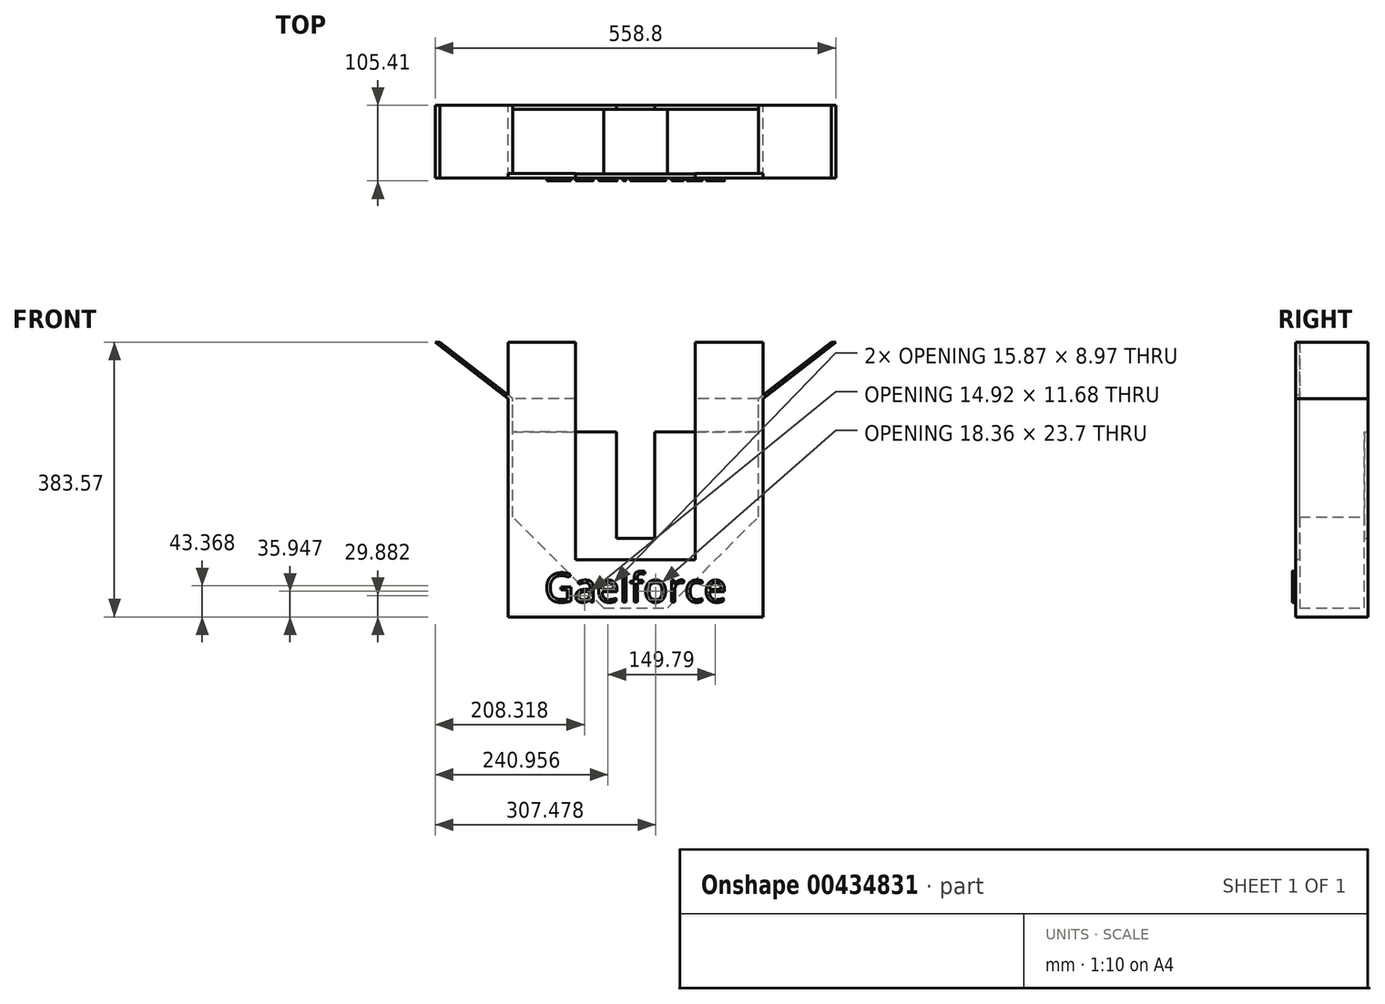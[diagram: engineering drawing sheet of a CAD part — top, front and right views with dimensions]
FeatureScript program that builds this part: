
annotation { "Feature Type Name" : "Feature", "Feature Type Description" : "" }
export const myFeature = defineFeature(function(context is Context, id is Id, definition is map)
    precondition{}
    {
        {
            var Q0;
            Q0=qCreatedBy(makeId("Front.planeOp"),FACE);
            var sketch = newSketch(context, id + "F0", { "sketchPlane" : qUnion([Q0])});
            skLineSegment(sketch, "E0.bottom", {"start": v(177.8, 152.4) * mm, "end": v(-177.8, 152.4) * mm});
            skLineSegment(sketch, "E0.top", {"start": v(177.8, -152.4) * mm, "end": v(-177.8, -152.4) * mm});
            skLineSegment(sketch, "E0.left", {"start": v(177.8, 152.4) * mm, "end": v(177.8, -152.4) * mm});
            skLineSegment(sketch, "E0.right", {"start": v(-177.8, 152.4) * mm, "end": v(-177.8, -152.4) * mm});
            skPoint(sketch, "E0.middle", {"position": v(0, 0) * mm});
            skSolve(sketch);
        }
        {
            var Q0;
            Q0=makeQuery(id+"F0.imprint","IMPRINT",FACE,{"disambiguationData":[TD([[makeQuery(id+"F0.imprint","IMPRINT",EDGE,{"derivedFrom":sQuery(id+"F0.wireOp",EDGE,"E0.bottom")}),1.0]])]});
            extrude(context, id + "F1", {"entities" : qUnion([Q0]), "endBound" : BoundingType.SYMMETRIC, "depth" : 101.6 * mm});
        }
        {
            var Q0;
            Q0=makeQuery(id+"F1.opExtrude","SWEPT_FACE",FACE,{"disambiguationData":[OSD([sQuery(id+"F0.wireOp",EDGE,"E0.bottom")])]});
            var sketch = newSketch(context, id + "F2", { "sketchPlane" : qUnion([Q0])});
            skLineSegment(sketch, "E1.bottom", {"start": v(-171.45, -44.94) * mm, "end": v(171.45, -44.94) * mm});
            skLineSegment(sketch, "E1.top", {"start": v(-171.45, 45.23) * mm, "end": v(171.45, 45.23) * mm});
            skLineSegment(sketch, "E1.left", {"start": v(-171.45, -44.94) * mm, "end": v(-171.45, 45.23) * mm});
            skLineSegment(sketch, "E1.right", {"start": v(171.45, -44.94) * mm, "end": v(171.45, 45.23) * mm});
            skSolve(sketch);
        }
        {
            var Q0;
            Q0=makeQuery(id+"F2.imprint","IMPRINT",FACE,{"disambiguationData":[TD([[makeQuery(id+"F2.imprint","IMPRINT",EDGE,{"derivedFrom":sQuery(id+"F2.wireOp",EDGE,"E1.bottom")}),1.0]])]});
            extrude(context, id + "F3", {"entities" : qUnion([Q0]), "operationType" : NewBodyOperationType.REMOVE, "oppositeDirection" : true, "depth" : 292.1 * mm});
        }
        {
            var Q0;
            Q0=makeQuery(id+"F1.opExtrude","SWEPT_FACE",FACE,{"disambiguationData":[OSD([sQuery(id+"F0.wireOp",EDGE,"E0.bottom")])]});
            var sketch = newSketch(context, id + "F4", { "sketchPlane" : qUnion([Q0])});
            skLineSegment(sketch, "E2", {"start": v(-171.45, 45.23) * mm, "end": v(-171.45, 50.8) * mm});
            skLineSegment(sketch, "E3", {"start": v(171.45, 45.23) * mm, "end": v(171.45, 50.8) * mm});
            skSolve(sketch);
        }
        {
            var Q0;
            {var subQ0=sQuery(id+"F4.wireOp",EDGE,"E2");Q0=makeQuery(id+"F4.imprint","IMPRINT",FACE,{"disambiguationData":[TD([[makeQuery(id+"F4.imprint","IMPRINT",EDGE,{"derivedFrom":subQ0}),-1.0]])]});}
            extrude(context, id + "F5", {"entities" : qUnion([Q0]), "operationType" : NewBodyOperationType.REMOVE, "oppositeDirection" : true, "depth" : 46.48 * mm});
        }
        {
            var Q0;
            Q0=makeQuery(id+"F1.opExtrude","CAP_FACE",FACE,{"disambiguationData":[OSD([sQuery(id+"F0.wireOp",EDGE,"E0.bottom"),sQuery(id+"F0.wireOp",EDGE,"E0.top"),sQuery(id+"F0.wireOp",EDGE,"E0.left"),sQuery(id+"F0.wireOp",EDGE,"E0.right")])],"isStart":false});
            var sketch = newSketch(context, id + "F6", { "sketchPlane" : qUnion([Q0])});
            skLineSegment(sketch, "E4.bottom", {"start": v(-83.6, -72.67) * mm, "end": v(83.6, -72.67) * mm});
            skLineSegment(sketch, "E4.top", {"start": v(-83.6, 377.47) * mm, "end": v(83.6, 377.47) * mm});
            skLineSegment(sketch, "E4.left", {"start": v(-83.6, -72.67) * mm, "end": v(-83.6, 377.47) * mm});
            skLineSegment(sketch, "E4.right", {"start": v(83.6, -72.67) * mm, "end": v(83.6, 377.47) * mm});
            skPoint(sketch, "E4.middle", {"position": v(0, 152.4) * mm});
            skSolve(sketch);
        }
        {
            var Q0;
            {var subQ0=sQuery(id+"F6.wireOp",EDGE,"E4.top");Q0=makeQuery(id+"F6.imprint","IMPRINT",FACE,{"disambiguationData":[TD([[makeQuery(id+"F6.imprint","IMPRINT",EDGE,{"derivedFrom":subQ0}),-1.0]])]});}
            var Q1;
            {var subQ0=sQuery(id+"F6.wireOp",EDGE,"E4.bottom");Q1=makeQuery(id+"F6.imprint","IMPRINT",FACE,{"disambiguationData":[TD([[makeQuery(id+"F6.imprint","IMPRINT",EDGE,{"derivedFrom":subQ0}),1.0]])]});}
            extrude(context, id + "F7", {"entities" : qUnion([Q0, Q1]), "operationType" : NewBodyOperationType.REMOVE, "oppositeDirection" : true, "depth" : 25.4 * mm});
        }
        {
            var Q0;
            Q0=makeQuery(id+"F1.opExtrude","CAP_FACE",FACE,{"disambiguationData":[OSD([sQuery(id+"F0.wireOp",EDGE,"E0.bottom"),sQuery(id+"F0.wireOp",EDGE,"E0.top"),sQuery(id+"F0.wireOp",EDGE,"E0.left"),sQuery(id+"F0.wireOp",EDGE,"E0.right")])],"isStart":false});
            var sketch = newSketch(context, id + "F8", { "sketchPlane" : qUnion([Q0])});
            skText(sketch, "E5", { "text": "Gaelforce", "fontName": "OpenSans-Regular.ttf"});
            const initialGuessF8  = {"E5": [-0.12725, -0.1316, 1, 0, 0.04083]};
            skSetInitialGuess(sketch, initialGuessF8);
            skSolve(sketch);
        }
        {
            var Q0;
            Q0 = qSketchRegion(id + "F8", true);
            extrude(context, id + "F9", {"entities" : qUnion([Q0]), "depth" : 3.8 * mm});
        }
        {
            var Q0;
            Q0=makeQuery(id+"F1.opExtrude","CAP_FACE",FACE,{"disambiguationData":[OSD([sQuery(id+"F0.wireOp",EDGE,"E0.bottom"),sQuery(id+"F0.wireOp",EDGE,"E0.top"),sQuery(id+"F0.wireOp",EDGE,"E0.left"),sQuery(id+"F0.wireOp",EDGE,"E0.right")])],"isStart":true});
            var sketch = newSketch(context, id + "F10", { "sketchPlane" : qUnion([Q0])});
            skLineSegment(sketch, "E6.bottom", {"start": v(-26.6, -43.01) * mm, "end": v(26.6, -43.01) * mm});
            skLineSegment(sketch, "E6.top", {"start": v(-26.6, 254.85) * mm, "end": v(26.6, 254.85) * mm});
            skLineSegment(sketch, "E6.left", {"start": v(-26.6, -43.01) * mm, "end": v(-26.6, 254.85) * mm});
            skLineSegment(sketch, "E6.right", {"start": v(26.6, -43.01) * mm, "end": v(26.6, 254.85) * mm});
            skPoint(sketch, "E6.middle", {"position": v(0, 105.92) * mm});
            skSolve(sketch);
        }
        {
            var Q0;
            {var subQ0=sQuery(id+"F10.wireOp",EDGE,"E6.bottom");Q0=makeQuery(id+"F10.imprint","IMPRINT",FACE,{"disambiguationData":[TD([[makeQuery(id+"F10.imprint","IMPRINT",EDGE,{"derivedFrom":subQ0}),1.0]])]});}
            extrude(context, id + "F11", {"entities" : qUnion([Q0]), "operationType" : NewBodyOperationType.REMOVE, "oppositeDirection" : true, "depth" : 25.4 * mm});
        }
        {
            var Q0;
            Q0=makeQuery(id+"F3.boolean.opBoolean","COPY",EDGE,{"derivedFrom":makeQuery(id+"F3.opExtrude","CAP_EDGE",EDGE,{"disambiguationData":[OSD([sQuery(id+"F2.wireOp",EDGE,"E1.left")])],"isStart":false})});
            var Q1;
            Q1=makeQuery(id+"F3.boolean.opBoolean","COPY",EDGE,{"derivedFrom":makeQuery(id+"F3.opExtrude","CAP_EDGE",EDGE,{"disambiguationData":[OSD([sQuery(id+"F2.wireOp",EDGE,"E1.right")])],"isStart":false})});
            chamfer(context, id + "F12", {"entities" : qUnion([Q0, Q1]), "width" : 127 * mm, "tangentPropagation" : true});
        }
        {
            var Q0;
            {var subQ0=sQuery(id+"F0.wireOp",EDGE,"E0.bottom");var subQ1=sQuery(id+"F0.wireOp",EDGE,"E0.left");var subQ2=sQuery(id+"F0.wireOp",EDGE,"E0.right");var subQ3=sQuery(id+"F0.wireOp",EDGE,"E0.top");Q0=makeQuery(id+"F9.boolean.opBoolean","SPLIT",FACE,{"disambiguationData":[TD([makeQuery(id+"F1.opExtrude","SWEPT_FACE",FACE,{"disambiguationData":[OSD([subQ0])]})])],"derivedFrom":makeQuery(id+"F1.opExtrude","CAP_FACE",FACE,{"disambiguationData":[OSD([subQ0,subQ3,subQ1,subQ2])],"isStart":false})});}
            var sketch = newSketch(context, id + "F13", { "sketchPlane" : qUnion([Q0])});
            skLineSegment(sketch, "E7.bottom", {"start": v(-279.4, 152.4) * mm, "end": v(279.4, 152.4) * mm});
            skLineSegment(sketch, "E7.top", {"start": v(-279.4, 231.17) * mm, "end": v(279.4, 231.17) * mm});
            skLineSegment(sketch, "E7.left", {"start": v(-279.4, 152.4) * mm, "end": v(-279.4, 231.17) * mm});
            skLineSegment(sketch, "E7.right", {"start": v(279.4, 152.4) * mm, "end": v(279.4, 231.17) * mm});
            skSolve(sketch);
        }
        {
            var Q0;
            Q0=makeQuery(id+"F13.imprint","IMPRINT",FACE,{"disambiguationData":[TD([[makeQuery(id+"F13.imprint","IMPRINT",EDGE,{"derivedFrom":sQuery(id+"F13.wireOp",EDGE,"E7.top")}),-1.0]])]});
            extrude(context, id + "F14", {"entities" : qUnion([Q0]), "operationType" : NewBodyOperationType.ADD, "oppositeDirection" : true, "depth" : 101.6 * mm});
        }
        {
            var Q0;
            {var subQ0=sQuery(id+"F0.wireOp",EDGE,"E0.bottom");var subQ1=sQuery(id+"F0.wireOp",EDGE,"E0.left");var subQ2=sQuery(id+"F0.wireOp",EDGE,"E0.right");var subQ3=sQuery(id+"F0.wireOp",EDGE,"E0.top");Q0=makeQuery(id+"F14.boolean.opBoolean","MERGE",FACE,{"derivedFrom":[makeQuery(id+"F9.boolean.opBoolean","SPLIT",FACE,{"disambiguationData":[TD([makeQuery(id+"F1.opExtrude","SWEPT_FACE",FACE,{"disambiguationData":[OSD([subQ0])]})])],"derivedFrom":makeQuery(id+"F1.opExtrude","CAP_FACE",FACE,{"disambiguationData":[OSD([subQ0,subQ3,subQ1,subQ2])],"isStart":false})}),makeQuery(id+"F14.opExtrude","CAP_FACE",FACE,{"disambiguationData":[OSD([sQuery(id+"F13.wireOp",EDGE,"E7.bottom"),sQuery(id+"F13.wireOp",EDGE,"E7.top"),sQuery(id+"F13.wireOp",EDGE,"E7.left"),sQuery(id+"F13.wireOp",EDGE,"E7.right")])],"isStart":true})]});}
            var sketch = newSketch(context, id + "F15", { "sketchPlane" : qUnion([Q0])});
            skLineSegment(sketch, "E8", {"start": v(-177.8, 152.4) * mm, "end": v(-279.4, 231.17) * mm});
            skLineSegment(sketch, "E9", {"start": v(177.8, 152.4) * mm, "end": v(279.4, 231.17) * mm});
            skLineSegment(sketch, "E10", {"start": v(177.8, 152.4) * mm, "end": v(83.6, 152.4) * mm});
            skLineSegment(sketch, "E11", {"start": v(83.6, 152.4) * mm, "end": v(-177.8, 152.4) * mm});
            skLineSegment(sketch, "E12", {"start": v(177.8, 231.17) * mm, "end": v(177.8, 152.4) * mm});
            skLineSegment(sketch, "E13", {"start": v(-177.8, 152.4) * mm, "end": v(-177.8, 231.17) * mm});
            skLineSegment(sketch, "E14", {"start": v(171.45, 152.4) * mm, "end": v(273.05, 231.17) * mm});
            skLineSegment(sketch, "E15", {"start": v(-171.45, 152.4) * mm, "end": v(-273.05, 231.17) * mm});
            skLineSegment(sketch, "E16", {"start": v(-83.6, 152.4) * mm, "end": v(-83.6, 231.17) * mm});
            skLineSegment(sketch, "E17", {"start": v(83.6, 152.4) * mm, "end": v(83.6, 231.17) * mm});
            skSolve(sketch);
        }
        {
            var Q0;
            Q0=makeQuery(id+"F15.imprint","IMPRINT",FACE,{"disambiguationData":[TD([[makeQuery(id+"F15.imprint","IMPRINT",EDGE,{"derivedFrom":sQuery(id+"F15.wireOp",EDGE,"E8")}),1.0]])]});
            var Q1;
            Q1=makeQuery(id+"F15.imprint","IMPRINT",FACE,{"disambiguationData":[TD([[makeQuery(id+"F15.imprint","IMPRINT",EDGE,{"derivedFrom":sQuery(id+"F15.wireOp",EDGE,"E9")}),-1.0]])]});
            var Q2;
            {var subQ0=sQuery(id+"F15.wireOp",EDGE,"E12");var subQ1=makeQuery(id+"F14.opExtrude","CAP_EDGE",EDGE,{"disambiguationData":[OSD([sQuery(id+"F13.wireOp",EDGE,"E7.top")])],"isStart":true});var subQ2=makeQuery(id+"F15.imprint","INTERSECT",VERTEX,{"derivedFrom":[subQ1,subQ0]});Q2=makeQuery(id+"F15.imprint","IMPRINT",FACE,{"disambiguationData":[TD([[makeQuery(id+"F15.imprint","IMPRINT",EDGE,{"disambiguationData":[TD([[subQ2,-1.0]])],"derivedFrom":subQ0}),1.0]])]});}
            var Q3;
            {var subQ0=sQuery(id+"F15.wireOp",EDGE,"E13");var subQ1=makeQuery(id+"F14.opExtrude","CAP_EDGE",EDGE,{"disambiguationData":[OSD([sQuery(id+"F13.wireOp",EDGE,"E7.top")])],"isStart":true});var subQ2=makeQuery(id+"F15.imprint","INTERSECT",VERTEX,{"derivedFrom":[subQ1,subQ0]});Q3=makeQuery(id+"F15.imprint","IMPRINT",FACE,{"disambiguationData":[TD([[makeQuery(id+"F15.imprint","IMPRINT",EDGE,{"disambiguationData":[TD([[subQ2,1.0]])],"derivedFrom":subQ0}),1.0]])]});}
            extrude(context, id + "F16", {"entities" : qUnion([Q0, Q1, Q2, Q3]), "operationType" : NewBodyOperationType.REMOVE, "oppositeDirection" : true, "depth" : 159.26 * mm});
        }
        {
            var Q0;
            {var subQ0=sQuery(id+"F15.wireOp",EDGE,"E16");Q0=makeQuery(id+"F15.imprint","IMPRINT",FACE,{"disambiguationData":[TD([[makeQuery(id+"F15.imprint","IMPRINT",EDGE,{"derivedFrom":subQ0}),-1.0]])]});}
            extrude(context, id + "F17", {"entities" : qUnion([Q0]), "operationType" : NewBodyOperationType.REMOVE, "oppositeDirection" : true, "depth" : 313.18 * mm});
        }
        {
            var Q0;
            Q0=makeQuery(id+"F14.boolean.opBoolean","MERGE",FACE,{"derivedFrom":[makeQuery(id+"F1.opExtrude","CAP_FACE",FACE,{"disambiguationData":[OSD([sQuery(id+"F0.wireOp",EDGE,"E0.bottom"),sQuery(id+"F0.wireOp",EDGE,"E0.top"),sQuery(id+"F0.wireOp",EDGE,"E0.left"),sQuery(id+"F0.wireOp",EDGE,"E0.right")])],"isStart":true}),makeQuery(id+"F14.opExtrude","CAP_FACE",FACE,{"disambiguationData":[OSD([sQuery(id+"F13.wireOp",EDGE,"E7.bottom"),sQuery(id+"F13.wireOp",EDGE,"E7.top"),sQuery(id+"F13.wireOp",EDGE,"E7.left"),sQuery(id+"F13.wireOp",EDGE,"E7.right")])],"isStart":false})]});
            var sketch = newSketch(context, id + "F18", { "sketchPlane" : qUnion([Q0])});
            skLineSegment(sketch, "E18", {"start": v(-177.8, 157.32) * mm, "end": v(-171.45, 152.4) * mm});
            skLineSegment(sketch, "E19", {"start": v(-171.45, 152.4) * mm, "end": v(171.45, 152.4) * mm});
            skLineSegment(sketch, "E20", {"start": v(171.45, 152.4) * mm, "end": v(177.8, 157.32) * mm});
            skSolve(sketch);
        }
        {
            var Q0;
            {var subQ9=sQuery(id+"F18.wireOp",EDGE,"E18");Q0=makeQuery(id+"F18.imprint","IMPRINT",FACE,{"disambiguationData":[TD([[makeQuery(id+"F18.imprint","IMPRINT",EDGE,{"derivedFrom":subQ9}),1.0]])]});}
            var Q1;
            {var subQ0=sQuery(id+"F18.wireOp",EDGE,"E20");Q1=makeQuery(id+"F18.imprint","IMPRINT",FACE,{"disambiguationData":[TD([[makeQuery(id+"F18.imprint","IMPRINT",EDGE,{"derivedFrom":subQ0}),1.0]])]});}
            extrude(context, id + "F19", {"entities" : qUnion([Q0, Q1]), "operationType" : NewBodyOperationType.REMOVE, "oppositeDirection" : true, "depth" : 95.25 * mm});
        }
    });
